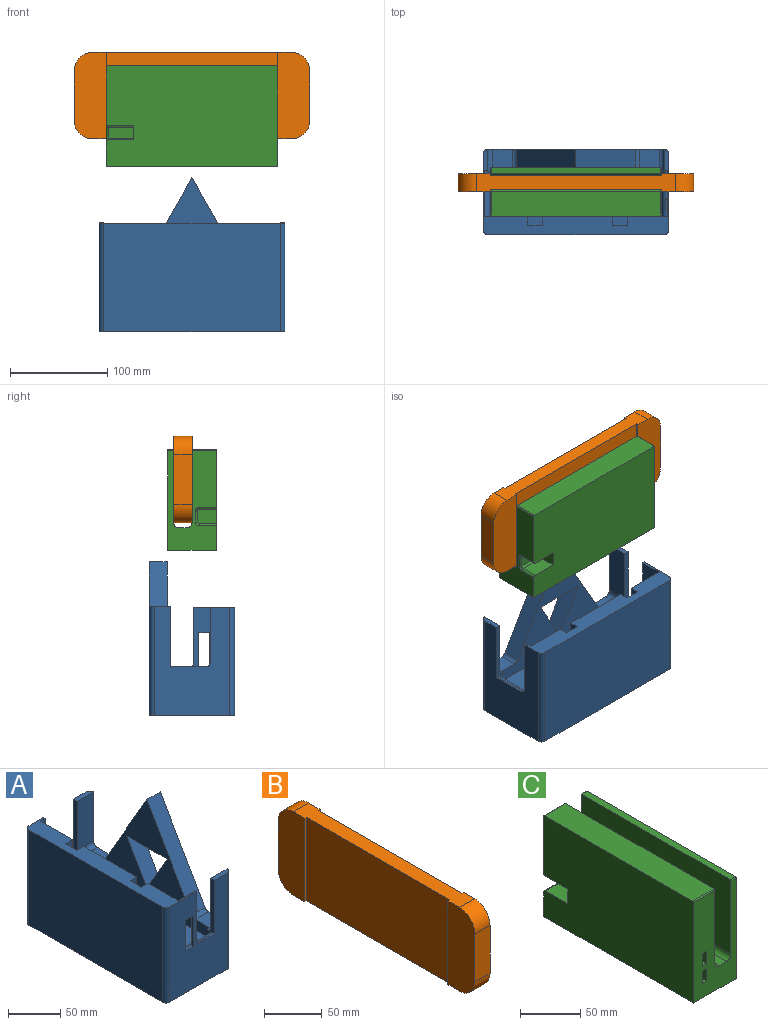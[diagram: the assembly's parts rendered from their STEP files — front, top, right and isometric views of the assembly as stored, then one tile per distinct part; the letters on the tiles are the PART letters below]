
ASSEMBLY  parts=3 mates=2
PART A: 120 faces, bbox 87.5x191x157.9 mm
  f0: plane 74x72.16mm, normal (1,0,0), area 5339.8mm2, adj f2,f19,f111,f116
  f1: plane 74x40.63mm, normal (1,0,0), area 2949.8mm2, adj f2,f4,f5,f16,f19,f113
  f2: plane 191x41.75mm, normal (0,0,1), area 3257.4mm2, adj f0,f1,f3,f5,f6,f13,f14,f22
  f3: plane 112.6x77.5mm, normal (0,-1,0), area 6832.2mm2, adj f2,f8,f15,f20,f23,f87,f98,f103
  f4: cylinder r=5mm len=51mm, axis (-1,0,0), area 381.8mm2, adj f1,f5,f8,f16,f17,f97,f105,f106
  f5: plane 61.5x28.5mm, normal (0,1,0), area 1072mm2, adj f1,f2,f4,f103,f104,f105,f107,f108
  f6: plane 74x43.74mm, normal (1,0,0), area 3179.8mm2, adj f2,f18,f19,f96,f101,f118
  f7: plane 35.4x2mm, normal (0,0,1), area 70.8mm2, adj f13,f96,f100,f109
  f8: plane 18.6x2mm, normal (0,0,1), area 37.2mm2, adj f3,f4,f98,f108
  f9: plane 20.31x18.25mm, normal (0,0,1), area 370.6mm2, adj f12,f17,f89,f94
  f10: plane 20.31x18.25mm, normal (0,0,1), area 370.6mm2, adj f12,f17,f90,f95
  f11: plane 57.6x22.15mm, normal (0,-1,0), area 1275.8mm2, adj f21,f88,f94,f100
  f12: plane 181x157.91mm, normal (1,0,0), area 13324.9mm2, adj f9,f10,f15,f20,f21,f24,f25,f26
  f13: plane 112.6x77.5mm, normal (0,1,0), area 6180.9mm2, adj f2,f7,f15,f21,f22,f88,f100,f102
  f14: plane 181x111.5mm, normal (-1,0,0), area 20181.5mm2, adj f2,f15,f22,f23
  f15: plane 191x87.5mm, normal (0,0,-1), area 16691mm2, adj f3,f12,f13,f14,f20,f21,f22,f23
  f16: plane 51x7.5mm, normal (0,1,0), area 382.5mm2, adj f1,f4,f17,f19
  f17: plane 187x120.41mm, normal (-1,0,0), area 7639.4mm2, adj f4,f9,f10,f16,f18,f19,f84,f85
  f18: plane 51x7.5mm, normal (0,-1,0), area 382.5mm2, adj f6,f17,f19,f96
  f19: plane 177x51mm, normal (0,0,1), area 9027mm2, adj f0,f1,f6,f16,f17,f18,f110,f117
  f20: cylinder r=5mm len=112.6mm, axis (0,0,-1), area 884.4mm2, adj f3,f12,f15,f86,f87
  f21: cylinder r=5mm len=112.6mm, axis (0,0,1), area 884.4mm2, adj f11,f12,f13,f15,f88
  f22: cylinder r=5mm len=111.5mm, axis (0,0,-1), area 875.7mm2, adj f2,f13,f14,f15
  f23: cylinder r=5mm len=111.5mm, axis (0,0,1), area 875.7mm2, adj f2,f3,f14,f15
  f24: plane 24x17mm, normal (0,0,1), area 408mm2, adj f12,f25,f27,f28
  f25: plane 17x4mm, normal (0,-1,0), area 68mm2, adj f12,f24,f26,f28
  f26: plane 24x17mm, normal (0,0,-1), area 408mm2, adj f12,f25,f27,f28
  f27: plane 17x4mm, normal (0,1,0), area 68mm2, adj f12,f24,f26,f28
  f28: plane 24x4mm, normal (1,0,0), area 96mm2, adj f24,f25,f26,f27
  f29: plane 24x17mm, normal (0,0,1), area 408mm2, adj f12,f30,f32,f33
  f30: plane 17x4mm, normal (0,-1,0), area 68mm2, adj f12,f29,f31,f33
  f31: plane 24x17mm, normal (0,0,-1), area 408mm2, adj f12,f30,f32,f33
  f32: plane 17x4mm, normal (0,1,0), area 68mm2, adj f12,f29,f31,f33
  f33: plane 24x4mm, normal (1,0,0), area 96mm2, adj f29,f30,f31,f32
  f34: plane 24x17mm, normal (0,0,1), area 408mm2, adj f12,f35,f37,f38
  f35: plane 17x4mm, normal (0,-1,0), area 68mm2, adj f12,f34,f36,f38
  f36: plane 24x17mm, normal (0,0,-1), area 408mm2, adj f12,f35,f37,f38
  f37: plane 17x4mm, normal (0,1,0), area 68mm2, adj f12,f34,f36,f38
  f38: plane 24x4mm, normal (1,0,0), area 96mm2, adj f34,f35,f36,f37
  f39: plane 24x17mm, normal (0,0,1), area 408mm2, adj f12,f40,f42,f43
  f40: plane 17x4mm, normal (0,-1,0), area 68mm2, adj f12,f39,f41,f43
  f41: plane 24x17mm, normal (0,0,-1), area 408mm2, adj f12,f40,f42,f43
  f42: plane 17x4mm, normal (0,1,0), area 68mm2, adj f12,f39,f41,f43
  f43: plane 24x4mm, normal (1,0,0), area 96mm2, adj f39,f40,f41,f42
  f44: plane 24x17mm, normal (0,0,1), area 408mm2, adj f12,f45,f47,f48
  f45: plane 17x4mm, normal (0,-1,0), area 68mm2, adj f12,f44,f46,f48
  f46: plane 24x17mm, normal (0,0,-1), area 408mm2, adj f12,f45,f47,f48
  f47: plane 17x4mm, normal (0,1,0), area 68mm2, adj f12,f44,f46,f48
  f48: plane 24x4mm, normal (1,0,0), area 96mm2, adj f44,f45,f46,f47
  f49: plane 24x17mm, normal (0,0,1), area 408mm2, adj f12,f50,f52,f53
  f50: plane 17x4mm, normal (0,-1,0), area 68mm2, adj f12,f49,f51,f53
  f51: plane 24x17mm, normal (0,0,-1), area 408mm2, adj f12,f50,f52,f53
  f52: plane 17x4mm, normal (0,1,0), area 68mm2, adj f12,f49,f51,f53
  f53: plane 24x4mm, normal (1,0,0), area 96mm2, adj f49,f50,f51,f52
  f54: plane 24x17mm, normal (0,0,1), area 408mm2, adj f12,f55,f57,f58
  f55: plane 17x4mm, normal (0,-1,0), area 68mm2, adj f12,f54,f56,f58
  f56: plane 24x17mm, normal (0,0,-1), area 408mm2, adj f12,f55,f57,f58
  f57: plane 17x4mm, normal (0,1,0), area 68mm2, adj f12,f54,f56,f58
  f58: plane 24x4mm, normal (1,0,0), area 96mm2, adj f54,f55,f56,f57
  f59: plane 24x17mm, normal (0,0,1), area 408mm2, adj f12,f60,f62,f63
  f60: plane 17x4mm, normal (0,-1,0), area 68mm2, adj f12,f59,f61,f63
  f61: plane 24x17mm, normal (0,0,-1), area 408mm2, adj f12,f60,f62,f63
  f62: plane 17x4mm, normal (0,1,0), area 68mm2, adj f12,f59,f61,f63
  f63: plane 24x4mm, normal (1,0,0), area 96mm2, adj f59,f60,f61,f62
  f64: plane 24x17mm, normal (0,0,1), area 408mm2, adj f12,f65,f67,f68
  f65: plane 17x4mm, normal (0,-1,0), area 68mm2, adj f12,f64,f66,f68
  f66: plane 24x17mm, normal (0,0,-1), area 408mm2, adj f12,f65,f67,f68
  f67: plane 17x4mm, normal (0,1,0), area 68mm2, adj f12,f64,f66,f68
  f68: plane 24x4mm, normal (1,0,0), area 96mm2, adj f64,f65,f66,f67
  f69: plane 24x17mm, normal (0,0,1), area 408mm2, adj f12,f70,f72,f73
  f70: plane 17x4mm, normal (0,-1,0), area 68mm2, adj f12,f69,f71,f73
  f71: plane 24x17mm, normal (0,0,-1), area 408mm2, adj f12,f70,f72,f73
  f72: plane 17x4mm, normal (0,1,0), area 68mm2, adj f12,f69,f71,f73
  f73: plane 24x4mm, normal (1,0,0), area 96mm2, adj f69,f70,f71,f72
  f74: plane 24x17mm, normal (0,0,1), area 408mm2, adj f12,f75,f77,f78
  f75: plane 17x4mm, normal (0,-1,0), area 68mm2, adj f12,f74,f76,f78
  f76: plane 24x17mm, normal (0,0,-1), area 408mm2, adj f12,f75,f77,f78
  f77: plane 17x4mm, normal (0,1,0), area 68mm2, adj f12,f74,f76,f78
  f78: plane 24x4mm, normal (1,0,0), area 96mm2, adj f74,f75,f76,f77
  f79: plane 24x17mm, normal (0,0,1), area 408mm2, adj f12,f80,f82,f83
  f80: plane 17x4mm, normal (0,-1,0), area 68mm2, adj f12,f79,f81,f83
  f81: plane 24x17mm, normal (0,0,-1), area 408mm2, adj f12,f80,f82,f83
  f82: plane 17x4mm, normal (0,1,0), area 68mm2, adj f12,f79,f81,f83
  f83: plane 24x4mm, normal (1,0,0), area 96mm2, adj f79,f80,f81,f82
  f84: plane 105.41x60.86mm, normal (0,-0.87,0.5), area 2221.4mm2, adj f12,f17,f85,f90
  f85: plane 105.41x60.86mm, normal (0,0.87,0.5), area 2221.4mm2, adj f12,f17,f84,f89
  f86: plane 57.6x22.15mm, normal (0,1,0), area 1275.8mm2, adj f20,f87,f95,f98
  f87: plane 22.15x5mm, normal (0,0,1), area 105.4mm2, adj f3,f20,f86,f98
  f88: plane 22.15x5mm, normal (0,0,1), area 105.4mm2, adj f11,f13,f21,f100
  f89: cylinder r=5mm len=18.25mm, axis (-1,0,0), area 95.6mm2, adj f9,f12,f17,f85
  f90: cylinder r=5mm len=18.25mm, axis (-1,0,0), area 95.6mm2, adj f10,f12,f17,f84
  f91: plane 55x18.25mm, normal (0,0,-1), area 1003.7mm2, adj f12,f17,f92,f93
  f92: plane 47.63x27.5mm, normal (0,0.87,0.5), area 1003.7mm2, adj f12,f17,f91,f93
  f93: plane 47.63x27.5mm, normal (0,-0.87,0.5), area 1003.7mm2, adj f12,f17,f91,f92
  f94: cylinder r=5mm len=22.15mm, axis (1,0,0), area 174mm2, adj f9,f11,f12,f99,f100
  f95: cylinder r=5mm len=22.15mm, axis (1,0,0), area 174mm2, adj f10,f12,f86,f97,f98
  f96: cylinder r=5mm len=51mm, axis (1,0,0), area 400.6mm2, adj f6,f7,f17,f18,f99,f101
  f97: plane 8x3.9mm, normal (0,0,-1), area 31.2mm2, adj f4,f17,f95,f98
  f98: plane 62.6x10mm, normal (-1,0,0), area 318.4mm2, adj f3,f8,f86,f87,f95,f97
  f99: plane 8x3.9mm, normal (0,0,-1), area 31.2mm2, adj f17,f94,f96,f100
  f100: plane 62.6x10mm, normal (-1,0,0), area 318.4mm2, adj f7,f11,f13,f88,f94,f99
  f101: plane 61.5x11.7mm, normal (0,-1,0), area 417.4mm2, adj f2,f6,f96,f102,f109
  f102: plane 56.5x2mm, normal (1,0,0), area 113mm2, adj f2,f13,f101,f109
  f103: plane 56.5x2mm, normal (1,0,0), area 113mm2, adj f2,f3,f5,f108
  f104: plane 10.72x2mm, normal (0,0,-1), area 21.4mm2, adj f3,f5,f105,f107
  f105: plane 35.6x3.71mm, normal (1,0,0), area 71.6mm2, adj f3,f4,f5,f104,f106
  f106: plane 10.72x3.71mm, normal (0,0,1), area 39.8mm2, adj f3,f4,f105,f107
  f107: plane 35.6x3.71mm, normal (-1,0,0), area 71.6mm2, adj f3,f4,f5,f104,f106
  f108: cylinder r=5mm len=5mm, axis (0,-1,0), area 15.7mm2, adj f3,f5,f8,f103
  f109: cylinder r=5mm len=5mm, axis (0,-1,0), area 15.7mm2, adj f7,f13,f101,f102
  f110: plane 15.23x4.5mm, normal (-1,0,0), area 68.5mm2, adj f19,f111,f113,f114
  f111: plane 78.5x9.13mm, normal (0,-1,0), area 716.3mm2, adj f0,f2,f110,f112,f114
  f112: plane 78.5x15.23mm, normal (1,0,0), area 1195.7mm2, adj f2,f111,f113,f114
  f113: plane 78.5x9.13mm, normal (0,1,0), area 716.3mm2, adj f1,f2,f110,f112,f114
  f114: plane 15.23x9.13mm, normal (0,0,1), area 139mm2, adj f110,f111,f112,f113
  f115: plane 78.5x15.23mm, normal (1,0,0), area 1195.7mm2, adj f2,f116,f118,f119
  f116: plane 78.5x9.13mm, normal (0,1,0), area 716.3mm2, adj f0,f2,f115,f117,f119
  f117: plane 15.23x4.5mm, normal (-1,0,0), area 68.5mm2, adj f19,f116,f118,f119
  f118: plane 78.5x9.13mm, normal (0,-1,0), area 716.3mm2, adj f2,f6,f115,f117,f119
  f119: plane 15.23x9.13mm, normal (0,0,1), area 139mm2, adj f115,f116,f117,f118
PART B: 18 faces, bbox 18.7x242x89 mm
  f0: plane 204x18.7mm, normal (0,0,-1), area 3075.6mm2, adj f4,f5,f6,f7,f8,f9,f10,f11
  f1: plane 51x18.7mm, normal (0,1,0), area 953.7mm2, adj f6,f9,f14,f15
  f2: plane 204x18.7mm, normal (0,0,1), area 3075.6mm2, adj f4,f5,f6,f7,f8,f9,f10,f11
  f3: plane 51x18.7mm, normal (0,-1,0), area 953.7mm2, adj f10,f13,f16,f17
  f4: plane 176x89mm, normal (1,0,0), area 15664mm2, adj f0,f2,f8,f12
  f5: plane 176x89mm, normal (-1,0,0), area 15664mm2, adj f0,f2,f7,f11
  f6: plane 89x33mm, normal (-1,0,0), area 2782.1mm2, adj f0,f1,f2,f7,f14,f15
  f7: plane 89x2.3mm, normal (0,-1,0), area 204.7mm2, adj f0,f2,f5,f6
  f8: plane 89x1.9mm, normal (0,-1,0), area 169.1mm2, adj f0,f2,f4,f9
  f9: plane 89x33mm, normal (1,0,0), area 2782.1mm2, adj f0,f1,f2,f8,f14,f15
  f10: plane 89x33mm, normal (-1,0,0), area 2782.1mm2, adj f0,f2,f3,f11,f16,f17
  f11: plane 89x2.3mm, normal (0,1,0), area 204.7mm2, adj f0,f2,f5,f10
  f12: plane 89x1.9mm, normal (0,1,0), area 169.1mm2, adj f0,f2,f4,f13
  f13: plane 89x33mm, normal (1,0,0), area 2782.1mm2, adj f0,f2,f3,f12,f16,f17
  f14: cylinder r=19mm len=19mm, axis (1,0,0), area 558.1mm2, adj f0,f1,f6,f9
  f15: cylinder r=19mm len=19mm, axis (-1,0,0), area 558.1mm2, adj f1,f2,f6,f9
  f16: cylinder r=19mm len=19mm, axis (1,0,0), area 558.1mm2, adj f2,f3,f10,f13
  f17: cylinder r=19mm len=19mm, axis (-1,0,0), area 558.1mm2, adj f0,f3,f10,f13
PART C: 37 faces, bbox 50x176x103 mm
  f0: plane 102x50mm, normal (0,-1,0), area 3504.5mm2, adj f3,f4,f6,f7,f8,f9,f11,f12
  f1: plane 102x50mm, normal (0,1,0), area 3227.5mm2, adj f3,f4,f6,f7,f8,f9,f10,f13
  f2: plane 174x25mm, normal (0,0,1), area 4350mm2, adj f3,f8,f12,f13
  f3: plane 176x103mm, normal (-1,0,0), area 17705.9mm2, adj f0,f1,f2,f6,f12,f13,f16,f18
  f4: plane 176x103mm, normal (1,0,0), area 18127.6mm2, adj f0,f1,f5,f6,f10,f11
  f5: plane 174x6.25mm, normal (0,0,1), area 1087.5mm2, adj f4,f7,f10,f11
  f6: plane 176x50mm, normal (0,0,-1), area 8800mm2, adj f0,f1,f3,f4
  f7: plane 176x75mm, normal (-1,0,0), area 13199.6mm2, adj f0,f1,f5,f10,f11,f14
  f8: plane 176x75mm, normal (1,0,0), area 13199.6mm2, adj f0,f1,f2,f12,f13,f15
  f9: plane 176x8.75mm, normal (0,0,1), area 1540mm2, adj f0,f1,f14,f15
  f10: cylinder r=1mm len=6.25mm, axis (1,0,0), area 9.8mm2, adj f1,f4,f5,f7
  f11: cylinder r=1mm len=6.25mm, axis (-1,0,0), area 9.8mm2, adj f0,f4,f5,f7
  f12: cylinder r=1mm len=25mm, axis (-1,0,0), area 39.3mm2, adj f0,f2,f3,f8
  f13: cylinder r=1mm len=25mm, axis (1,0,0), area 39.3mm2, adj f1,f2,f3,f8
  f14: cylinder r=5mm len=176mm, axis (0,1,0), area 1382.3mm2, adj f0,f1,f7,f9
  f15: cylinder r=5mm len=176mm, axis (0,-1,0), area 1382.3mm2, adj f0,f1,f8,f9
  f16: plane 26x17.52mm, normal (0,0,-1), area 455.4mm2, adj f3,f19,f23,f26
  f17: plane 26x11mm, normal (-1,0,0), area 286mm2, adj f19,f20,f23,f24
  f18: plane 26x17.52mm, normal (0,0,1), area 455.4mm2, adj f3,f19,f20,f21
  f19: plane 19.52x15mm, normal (0,1,0), area 291mm2, adj f3,f16,f17,f18,f20,f23
  f20: cylinder r=2mm len=26mm, axis (0,-1,0), area 81.7mm2, adj f17,f18,f19,f22
  f21: cylinder r=2mm len=17.52mm, axis (1,0,0), area 55mm2, adj f1,f3,f18,f22
  f22: torus R=4mm, axis (0,1,0), area 13.5mm2, adj f1,f20,f21,f24
  f23: cylinder r=2mm len=26mm, axis (0,-1,0), area 81.7mm2, adj f16,f17,f19,f25
  f24: cylinder r=2mm len=11mm, axis (0,0,1), area 34.6mm2, adj f1,f17,f22,f25
  f25: torus R=4mm, axis (0,1,0), area 13.5mm2, adj f1,f23,f24,f26
  f26: cylinder r=2mm len=17.52mm, axis (-1,0,0), area 55mm2, adj f1,f3,f16,f25
  f27: plane 25x5mm, normal (0,0,-1), area 125mm2, adj f0,f28,f30,f31
  f28: plane 25x12.5mm, normal (1,0,0), area 312.5mm2, adj f0,f27,f29,f31
  f29: plane 25x5mm, normal (0,0,1), area 125mm2, adj f0,f28,f30,f31
  f30: plane 25x12.5mm, normal (-1,0,0), area 312.5mm2, adj f0,f27,f29,f31
  f31: plane 12.5x5mm, normal (0,-1,0), area 62.5mm2, adj f27,f28,f29,f30
  f32: plane 25x5mm, normal (0,0,-1), area 125mm2, adj f0,f33,f35,f36
  f33: plane 25x12.5mm, normal (1,0,0), area 312.5mm2, adj f0,f32,f34,f36
  f34: plane 25x5mm, normal (0,0,1), area 125mm2, adj f0,f33,f35,f36
  f35: plane 25x12.5mm, normal (-1,0,0), area 312.5mm2, adj f0,f32,f34,f36
  f36: plane 12.5x5mm, normal (0,-1,0), area 62.5mm2, adj f32,f33,f34,f35
PLACE A rot(axis=(0,0,1),90deg) t=(0,0,50)mm
PLACE B rot(axis=(0,0,1),90deg) t=(0,0.16,174.2)mm
PLACE C rot(axis=(0,0,1),90deg) t=(0,0,169.9)mm
MATE slider C.f9 <-> B.f0  axis (0,0,1) through (0,9.38,192.9)mm
MATE slider C.f6 <-> A.f19  axis (0,0,-1) through (0,0,169.9)mm
